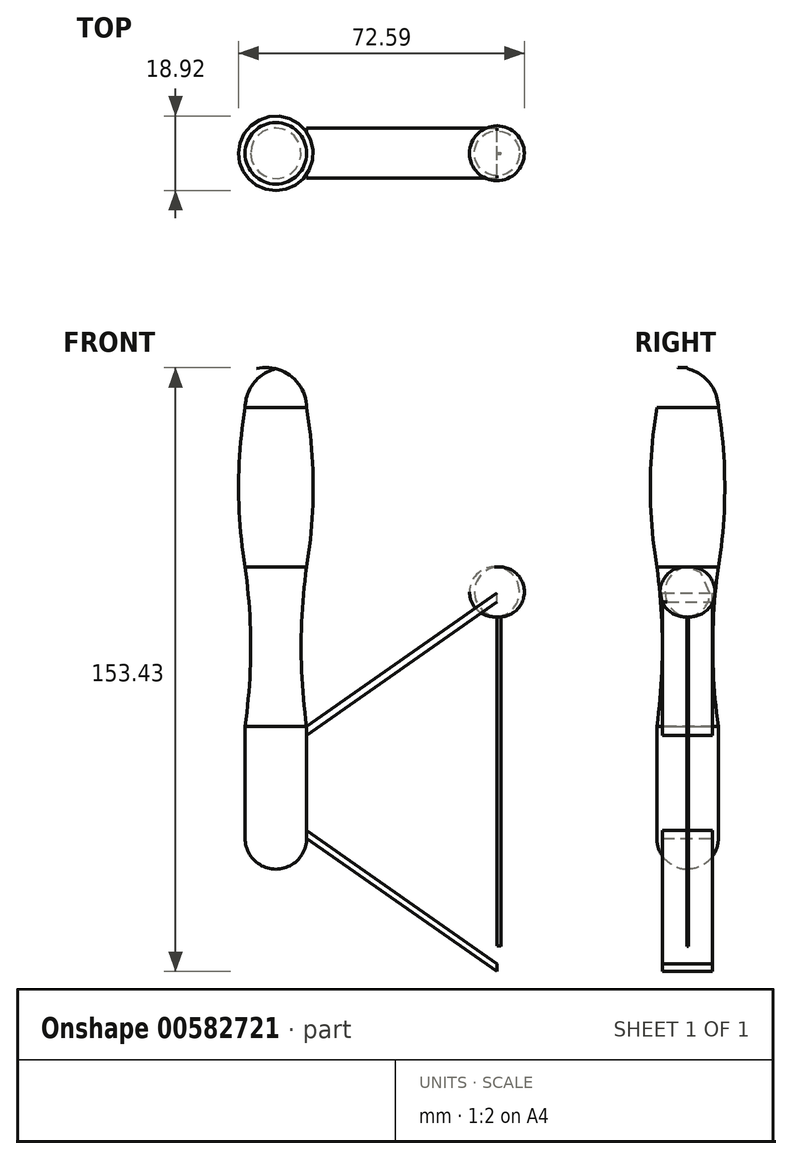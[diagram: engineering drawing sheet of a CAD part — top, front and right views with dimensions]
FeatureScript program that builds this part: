
annotation { "Feature Type Name" : "Feature", "Feature Type Description" : "" }
export const myFeature = defineFeature(function(context is Context, id is Id, definition is map)
    precondition{}
    {
        {
            var Q0;
            Q0=qCreatedBy(makeId("Front.planeOp"),FACE);
            var sketch = newSketch(context, id + "F0", { "sketchPlane" : qUnion([Q0])});
            skLineSegment(sketch, "E0", {"start": v(0, 0) * mm, "end": v(0, -40.5) * mm});
            skLineSegment(sketch, "E1", {"start": v(7.82, 0) * mm, "end": v(0, 0) * mm});
            skArc(sketch, "E2", {"start": v(7.82, 0) * mm, "mid": v(6.4, -20.25) * mm, "end": v(7.82, -40.5) * mm});
            skLineSegment(sketch, "E3", {"start": v(0, 0) * mm, "end": v(0, 40.5) * mm});
            skLineSegment(sketch, "E4", {"start": v(7.82, 40.5) * mm, "end": v(0, 40.5) * mm});
            skArc(sketch, "E5", {"start": v(7.82, 0) * mm, "mid": v(9.46, 20.25) * mm, "end": v(7.82, 40.5) * mm});
            skLineSegment(sketch, "E6", {"start": v(0, 40.5) * mm, "end": v(0, 50.36) * mm});
            skArc(sketch, "E7", {"start": v(7.82, 40.5) * mm, "mid": v(5.6, 46.77) * mm, "end": v(0, 50.36) * mm});
            skLineSegment(sketch, "E8", {"start": v(0, -40.5) * mm, "end": v(7.82, -40.5) * mm});
            skLineSegment(sketch, "E9", {"start": v(7.82, -40.5) * mm, "end": v(56.16, -6.64) * mm});
            skLineSegment(sketch, "E10", {"start": v(7.82, -68.92) * mm, "end": v(56.16, -102.77) * mm});
            skLineSegment(sketch, "E11", {"start": v(7.82, -68.92) * mm, "end": v(7.82, -40.5) * mm});
            skLineSegment(sketch, "E12", {"start": v(0, -40.5) * mm, "end": v(0, -68.92) * mm});
            skLineSegment(sketch, "E13", {"start": v(0, -68.92) * mm, "end": v(7.82, -68.92) * mm});
            skLineSegment(sketch, "E14", {"start": v(0, -68.92) * mm, "end": v(0, -76.78) * mm});
            skArc(sketch, "E15", {"start": v(0, -76.78) * mm, "mid": v(5.53, -74.46) * mm, "end": v(7.82, -68.92) * mm});
            skArc(sketch, "E16", {"start": v(56.16, -108.95) * mm, "mid": v(62.5, -102.6) * mm, "end": v(56.16, -96.25) * mm});
            skLineSegment(sketch, "E17", {"start": v(56.16, -96.25) * mm, "end": v(56.16, -12.64) * mm});
            skLineSegment(sketch, "E18", {"start": v(56.16, -108.95) * mm, "end": v(56.16, -96.25) * mm});
            skLineSegment(sketch, "E19", {"start": v(56.16, -12.64) * mm, "end": v(56.16, 0) * mm});
            skArc(sketch, "E20", {"start": v(56.16, -12.64) * mm, "mid": v(61.9, -6.32) * mm, "end": v(56.16, 0) * mm});
            skLineSegment(sketch, "E21", {"start": v(57.18, -96.33) * mm, "end": v(57.18, -12.46) * mm});
            skLineSegment(sketch, "E22", {"start": v(56.16, -100.78) * mm, "end": v(7.82, -66.93) * mm});
            skLineSegment(sketch, "E23", {"start": v(56.16, -8.88) * mm, "end": v(7.82, -42.73) * mm});
            skSolve(sketch);
        }
        {
            var Q0;
            Q0=makeQuery(id+"F0.imprint","IMPRINT",FACE,{"disambiguationData":[TD([[makeQuery(id+"F0.imprint","IMPRINT",EDGE,{"derivedFrom":sQuery(id+"F0.wireOp",EDGE,"E8")}),-1.0]])]});
            var Q1;
            Q1=makeQuery(id+"F0.imprint","IMPRINT",FACE,{"disambiguationData":[TD([[makeQuery(id+"F0.imprint","IMPRINT",EDGE,{"derivedFrom":sQuery(id+"F0.wireOp",EDGE,"E0")}),1.0]])]});
            var Q2;
            Q2=makeQuery(id+"F0.imprint","IMPRINT",FACE,{"disambiguationData":[TD([[makeQuery(id+"F0.imprint","IMPRINT",EDGE,{"derivedFrom":sQuery(id+"F0.wireOp",EDGE,"E1")}),-1.0]])]});
            var Q3;
            Q3=makeQuery(id+"F0.imprint","IMPRINT",FACE,{"disambiguationData":[TD([[makeQuery(id+"F0.imprint","IMPRINT",EDGE,{"derivedFrom":sQuery(id+"F0.wireOp",EDGE,"E4")}),-1.0]])]});
            var Q4;
            Q4=makeQuery(id+"F0.imprint","IMPRINT",FACE,{"disambiguationData":[TD([[makeQuery(id+"F0.imprint","IMPRINT",EDGE,{"derivedFrom":sQuery(id+"F0.wireOp",EDGE,"E13")}),-1.0]])]});
            var Q5;
            Q5=sQuery(id+"F0.wireOp",EDGE,"E3");
            revolve(context, id + "F1", {"entities" : qUnion([Q0, Q1, Q2, Q3, Q4]), "axis" : qUnion([Q5]), "revolveType" : RevolveType.FULL});
        }
        {
            var Q0;
            {var subQ0=sQuery(id+"F0.wireOp",EDGE,"E18");var subQ1=sQuery(id+"F0.wireOp",EDGE,"E16");var subQ2=makeQuery(id+"F0.imprint","INTERSECT",VERTEX,{"derivedFrom":[subQ1,subQ0]});Q0=makeQuery(id+"F0.imprint","IMPRINT",FACE,{"disambiguationData":[TD([[makeQuery(id+"F0.imprint","IMPRINT",EDGE,{"disambiguationData":[TD([[subQ2,-1.0]])],"derivedFrom":subQ1}),1.0]])]});}
            var Q1;
            {var subQ0=sQuery(id+"F0.wireOp",EDGE,"E19");var subQ1=makeQuery(id+"F0.imprint","INTERSECT",VERTEX,{"derivedFrom":[sQuery(id+"F0.wireOp",EDGE,"E9"),subQ0]});Q1=makeQuery(id+"F0.imprint","IMPRINT",FACE,{"disambiguationData":[TD([[makeQuery(id+"F0.imprint","IMPRINT",EDGE,{"disambiguationData":[TD([[subQ1,-1.0]])],"derivedFrom":subQ0}),-1.0]])]});}
            var Q2;
            Q2=sQuery(id+"F0.wireOp",EDGE,"E18");
            revolve(context, id + "F2", {"entities" : qUnion([Q0, Q1]), "axis" : qUnion([Q2]), "revolveType" : RevolveType.FULL});
        }
        {
            var Q0;
            {var subQ0=sQuery(id+"F0.wireOp",EDGE,"E17");Q0=makeQuery(id+"F0.imprint","IMPRINT",FACE,{"disambiguationData":[TD([[makeQuery(id+"F0.imprint","IMPRINT",EDGE,{"derivedFrom":subQ0}),-1.0]])]});}
            extrude(context, id + "F3", {"entities" : qUnion([Q0]), "operationType" : NewBodyOperationType.ADD, "endBound" : BoundingType.SYMMETRIC, "depth" : 0.38 * mm, "offsetDistance" : 25.4 * mm});
        }
        {
            var Q0;
            {var subQ0=sQuery(id+"F0.wireOp",EDGE,"E9");Q0=makeQuery(id+"F0.imprint","IMPRINT",FACE,{"disambiguationData":[TD([[makeQuery(id+"F0.imprint","IMPRINT",EDGE,{"derivedFrom":subQ0}),-1.0]])]});}
            var Q1;
            {var subQ0=sQuery(id+"F0.wireOp",EDGE,"E10");Q1=makeQuery(id+"F0.imprint","IMPRINT",FACE,{"disambiguationData":[TD([[makeQuery(id+"F0.imprint","IMPRINT",EDGE,{"derivedFrom":subQ0}),1.0]])]});}
            extrude(context, id + "F4", {"entities" : qUnion([Q0, Q1]), "endBound" : BoundingType.SYMMETRIC, "depth" : 12.7 * mm, "offsetDistance" : 25.4 * mm});
        }
    });
